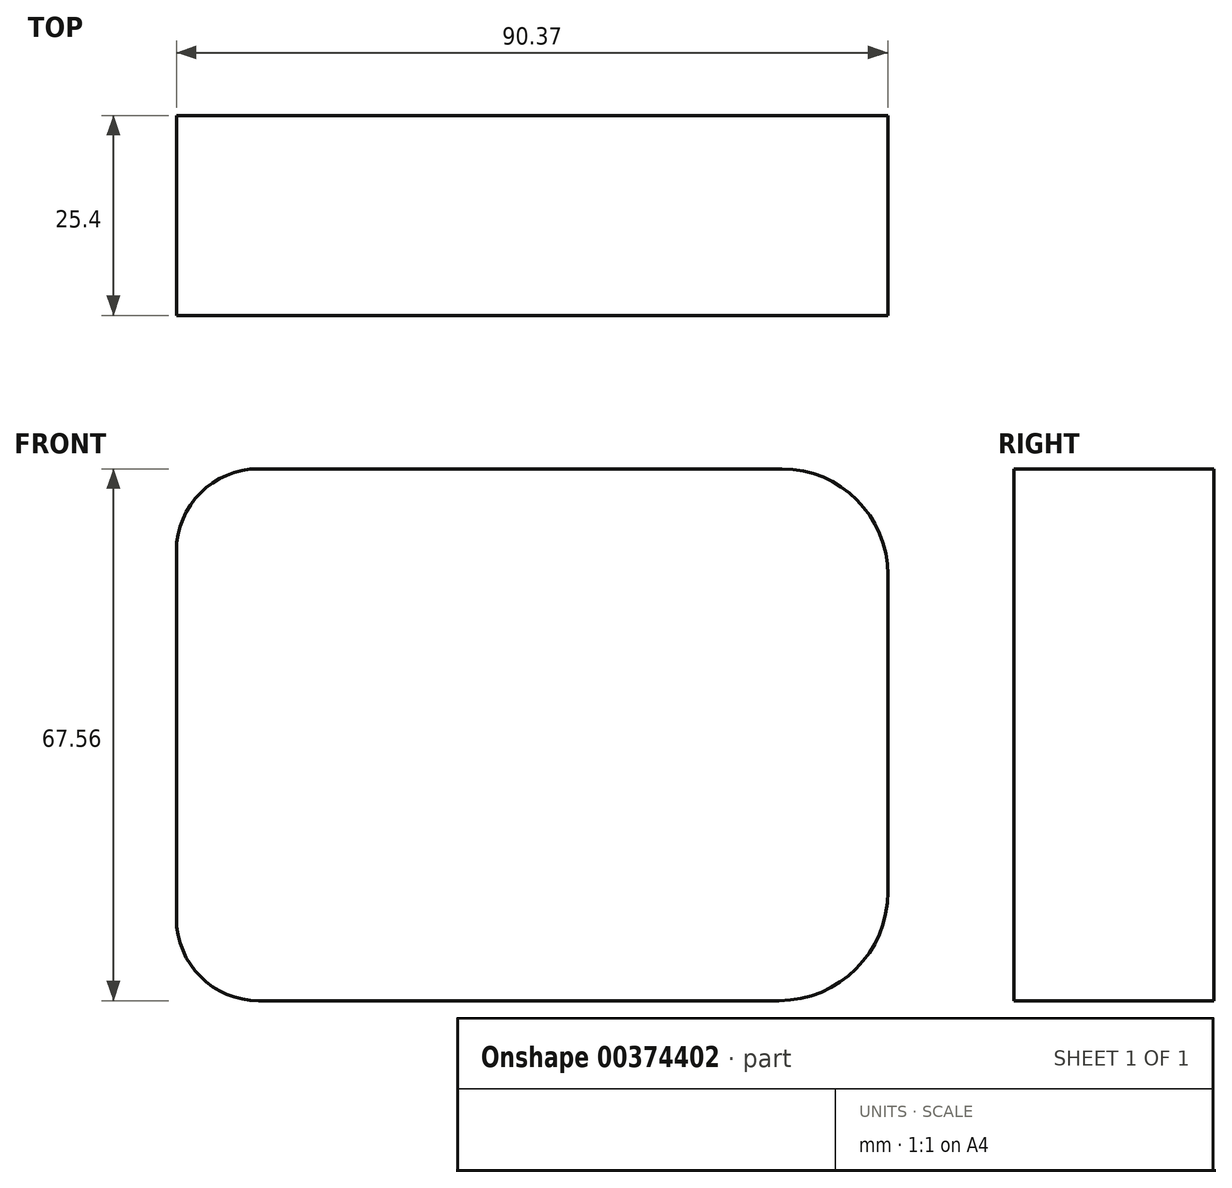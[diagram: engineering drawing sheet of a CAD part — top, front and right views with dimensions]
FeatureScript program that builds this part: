
annotation { "Feature Type Name" : "Feature", "Feature Type Description" : "" }
export const myFeature = defineFeature(function(context is Context, id is Id, definition is map)
    precondition{}
    {
        {
            var Q0;
            Q0=qCreatedBy(makeId("Front.planeOp"),FACE);
            var sketch = newSketch(context, id + "F0", { "sketchPlane" : qUnion([Q0])});
            skLineSegment(sketch, "E0.bottom", {"start": v(23.04, -37.07) * mm, "end": v(-43.08, -37.07) * mm});
            skLineSegment(sketch, "E0.top", {"start": v(23.4, 30.5) * mm, "end": v(-43.08, 30.5) * mm});
            skLineSegment(sketch, "E0.left", {"start": v(36.85, -23.26) * mm, "end": v(36.85, 17.04) * mm});
            skLineSegment(sketch, "E0.right", {"start": v(-53.52, -26.63) * mm, "end": v(-53.52, 20.05) * mm});
            skPoint(sketch, "E1.visualSharp", {"position": v(-53.52, 30.5) * mm});
            skArc(sketch, "E1.filletArc", {"start": v(-43.08, 30.5) * mm, "mid": v(-50.47, 27.43) * mm, "end": v(-53.52, 20.05) * mm});
            skPoint(sketch, "E2.visualSharp", {"position": v(36.85, -37.07) * mm});
            skArc(sketch, "E2.filletArc", {"start": v(23.04, -37.07) * mm, "mid": v(32.8, -33.03) * mm, "end": v(36.85, -23.26) * mm});
            skPoint(sketch, "E3.visualSharp", {"position": v(36.85, 30.5) * mm});
            skArc(sketch, "E3.filletArc", {"start": v(36.85, 17.04) * mm, "mid": v(32.91, 26.55) * mm, "end": v(23.4, 30.5) * mm});
            skPoint(sketch, "E4.visualSharp", {"position": v(-53.52, -37.07) * mm});
            skArc(sketch, "E4.filletArc", {"start": v(-53.52, -26.63) * mm, "mid": v(-50.47, -34.01) * mm, "end": v(-43.08, -37.07) * mm});
            skSolve(sketch);
        }
        {
            var Q0;
            Q0 = qSketchRegion(id + "F0", true);
            extrude(context, id + "F1", {"entities" : qUnion([Q0]), "depth" : 25.4 * mm});
        }
    });
